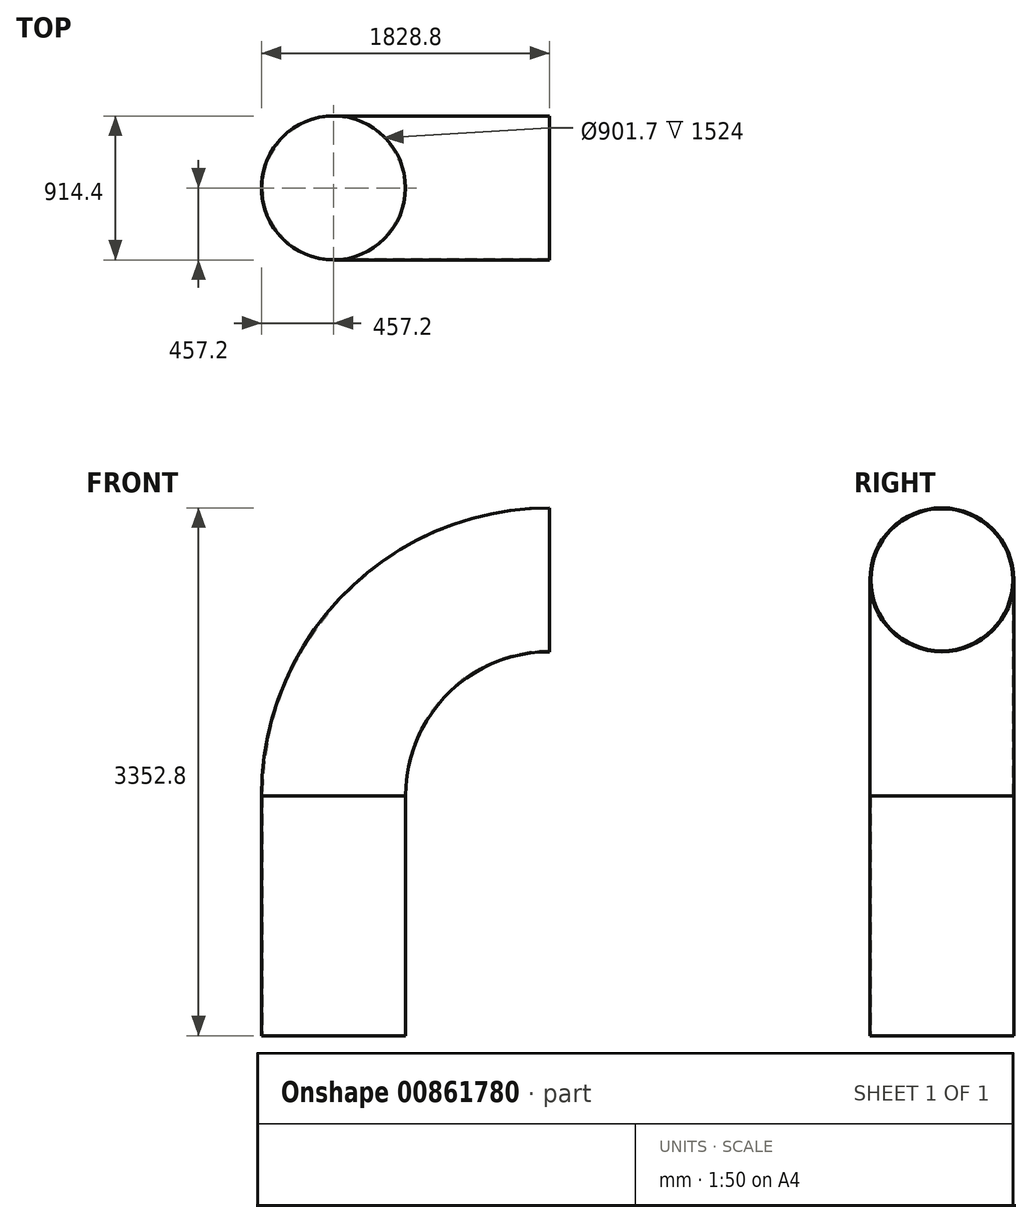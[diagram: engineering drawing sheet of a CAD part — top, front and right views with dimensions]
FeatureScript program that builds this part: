
annotation { "Feature Type Name" : "Feature", "Feature Type Description" : "" }
export const myFeature = defineFeature(function(context is Context, id is Id, definition is map)
    precondition{}
    {
        {
            var Q0;
            Q0=qCreatedBy(makeId("Top.planeOp"),FACE);
            var sketch = newSketch(context, id + "F0", { "sketchPlane" : qUnion([Q0])});
            skCircle(sketch, "E0", {"center": v(0, 0) * mm, "radius": 457.2 * mm});
            skCircle(sketch, "E1.0", {"center": v(0, 0) * mm, "radius": 450.85 * mm});
            skSolve(sketch);
        }
        {
            var Q0;
            Q0=makeQuery(id+"F0.imprint","IMPRINT",FACE,{"disambiguationData":[TD([[makeQuery(id+"F0.imprint","IMPRINT",EDGE,{"derivedFrom":sQuery(id+"F0.wireOp",EDGE,"E0")}),1.0]])]});
            extrude(context, id + "F1", {"entities" : qUnion([Q0]), "depth" : 1524 * mm, "offsetDistance" : 25.4 * mm});
        }
        {
            var Q0;
            Q0=makeQuery(id+"F1.opExtrude","CAP_FACE",FACE,{"disambiguationData":[OSD([sQuery(id+"F0.wireOp",EDGE,"E0"),sQuery(id+"F0.wireOp",EDGE,"E1.0")])],"isStart":false});
            var sketch = newSketch(context, id + "F2", { "sketchPlane" : qUnion([Q0])});
            skLineSegment(sketch, "E2", {"start": v(0, 0) * mm, "end": v(1371.6, 0) * mm, "construction": true});
            skLineSegment(sketch, "E3", {"start": v(1371.6, 0) * mm, "end": v(1371.6, 1368.93) * mm});
            skSolve(sketch);
        }
        {
            var Q0;
            Q0=makeQuery(id+"F2.imprint","IMPRINT",FACE,{"disambiguationData":[TD([[makeQuery(id+"F2.imprint","IMPRINT",EDGE,{"derivedFrom":makeQuery(id+"F1.opExtrude","CAP_EDGE",EDGE,{"disambiguationData":[OSD([sQuery(id+"F0.wireOp",EDGE,"E0")])],"isStart":false})}),1.0]])]});
            var Q1;
            Q1=sQuery(id+"F2.wireOp",EDGE,"E3");
            revolve(context, id + "F3", {"surfaceOperationType" : NewSurfaceOperationType.NEW, "entities" : qUnion([Q0]), "axis" : qUnion([Q1]), "revolveType" : RevolveType.ONE_DIRECTION, "angle" : 90 * degree});
        }
    });
